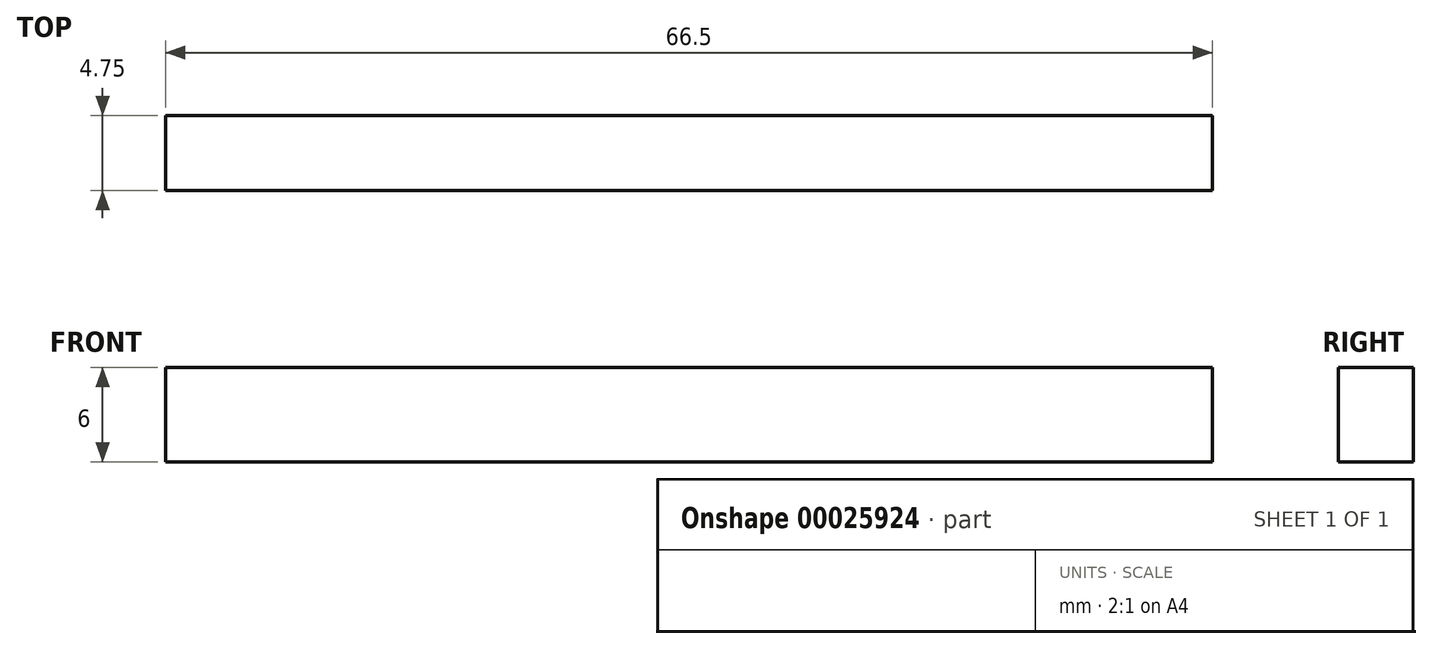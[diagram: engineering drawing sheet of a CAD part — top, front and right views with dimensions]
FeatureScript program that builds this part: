
annotation { "Feature Type Name" : "Feature", "Feature Type Description" : "" }
export const myFeature = defineFeature(function(context is Context, id is Id, definition is map)
    precondition{}
    {
        {
            var Q0;
            Q0=qCreatedBy(makeId("Front.planeOp"),FACE);
            var sketch = newSketch(context, id + "F0", { "sketchPlane" : qUnion([Q0])});
            skLineSegment(sketch, "E0.bottom", {"start": v(0, 0) * mm, "end": v(66.5, 0) * mm});
            skLineSegment(sketch, "E0.top", {"start": v(0, 6) * mm, "end": v(66.5, 6) * mm});
            skLineSegment(sketch, "E0.left", {"start": v(0, 0) * mm, "end": v(0, 6) * mm});
            skLineSegment(sketch, "E0.right", {"start": v(66.5, 0) * mm, "end": v(66.5, 6) * mm});
            skSolve(sketch);
        }
        {
            var Q0;
            Q0=makeQuery(id+"F0.imprint","IMPRINT",FACE,{"disambiguationData":[TD([[makeQuery(id+"F0.imprint","IMPRINT",EDGE,{"derivedFrom":sQuery(id+"F0.wireOp",EDGE,"E0.bottom")}),1.0]])]});
            extrude(context, id + "F1", {"entities" : qUnion([Q0]), "depth" : 4.75 * mm});
        }
    });
